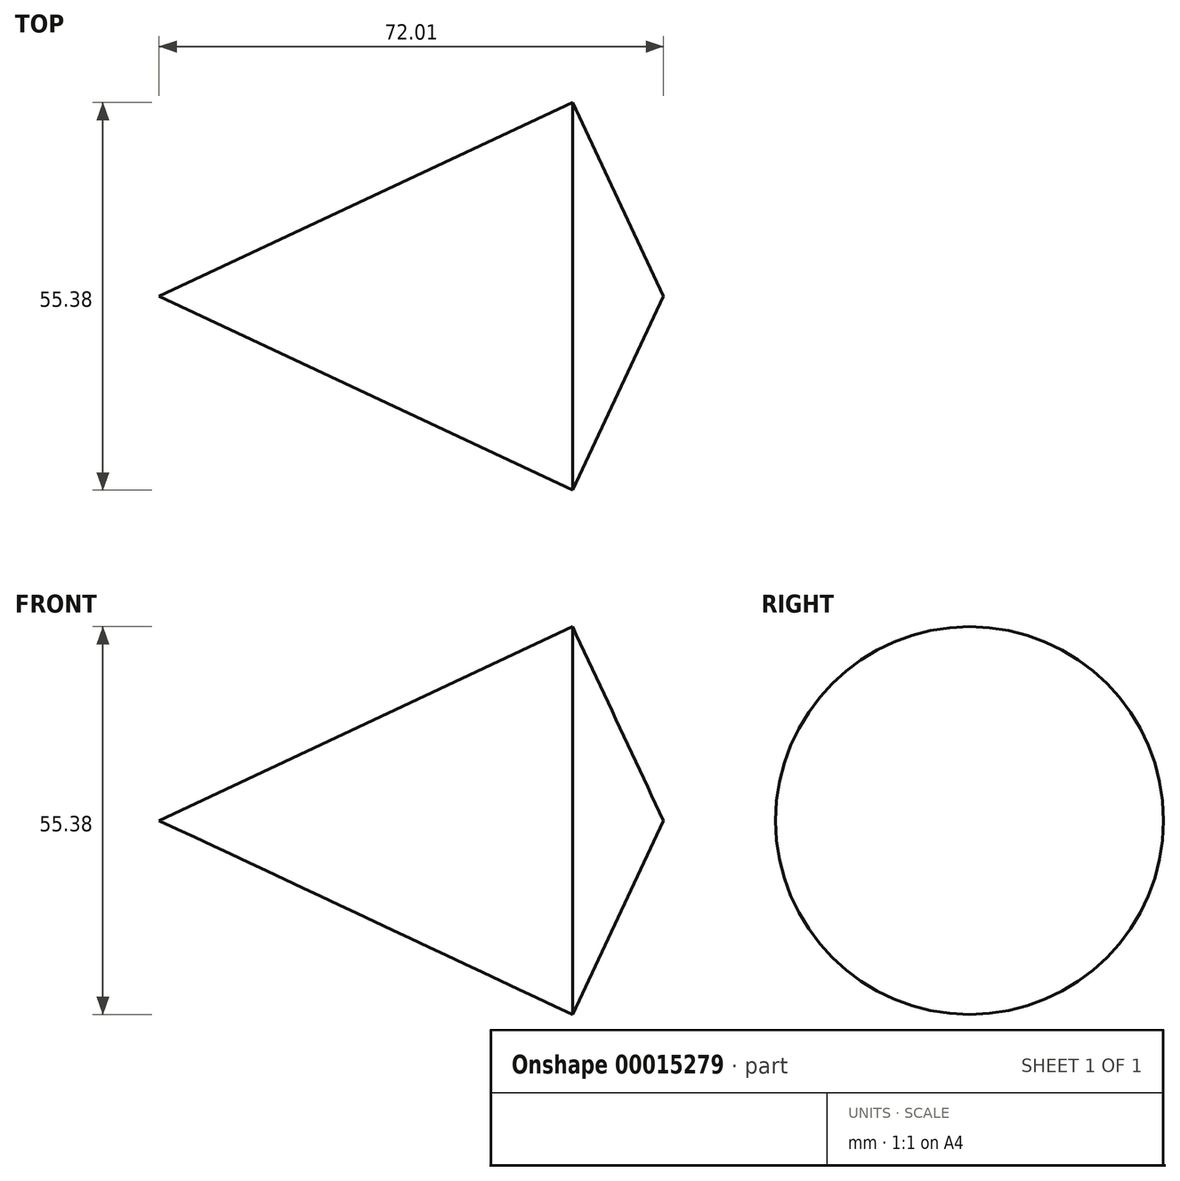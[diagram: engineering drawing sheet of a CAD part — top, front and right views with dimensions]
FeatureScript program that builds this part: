
annotation { "Feature Type Name" : "Feature", "Feature Type Description" : "" }
export const myFeature = defineFeature(function(context is Context, id is Id, definition is map)
    precondition{}
    {
        {
            var Q0;
            Q0=qCreatedBy(makeId("Front.planeOp"),FACE);
            var sketch = newSketch(context, id + "F0", { "sketchPlane" : qUnion([Q0])});
            skLineSegment(sketch, "E0", {"start": v(13.11, 27.95) * mm, "end": v(0, 0) * mm});
            skLineSegment(sketch, "E1", {"start": v(0, 0) * mm, "end": v(59.02, 27.69) * mm});
            skLineSegment(sketch, "E2", {"start": v(59.02, 27.69) * mm, "end": v(72, 0) * mm});
            skLineSegment(sketch, "E3", {"start": v(72, 0) * mm, "end": v(0, 0) * mm});
            skLineSegment(sketch, "E4", {"start": v(52.95, 23.55) * mm, "end": v(47.15, -33.6) * mm});
            skLineSegment(sketch, "E5", {"start": v(47.15, -33.6) * mm, "end": v(47.92, -25.94) * mm});
            skLineSegment(sketch, "E6", {"start": v(47.92, -25.94) * mm, "end": v(50.5, -27.9) * mm});
            skLineSegment(sketch, "E7", {"start": v(49.36, -11.82) * mm, "end": v(50.5, -27.9) * mm});
            skSolve(sketch);
        }
        {
            var Q0;
            {var subQ2=sQuery(id+"F0.wireOp",EDGE,"E1");Q0=makeQuery(id+"F0.imprint","IMPRINT",FACE,{"disambiguationData":[TD([[makeQuery(id+"F0.imprint","IMPRINT",EDGE,{"derivedFrom":subQ2}),-1.0]])]});}
            var Q1;
            Q1=sQuery(id+"F0.wireOp",EDGE,"E3");
            revolve(context, id + "F1", {"entities" : qUnion([Q0]), "axis" : qUnion([Q1]), "revolveType" : RevolveType.FULL});
        }
    });
